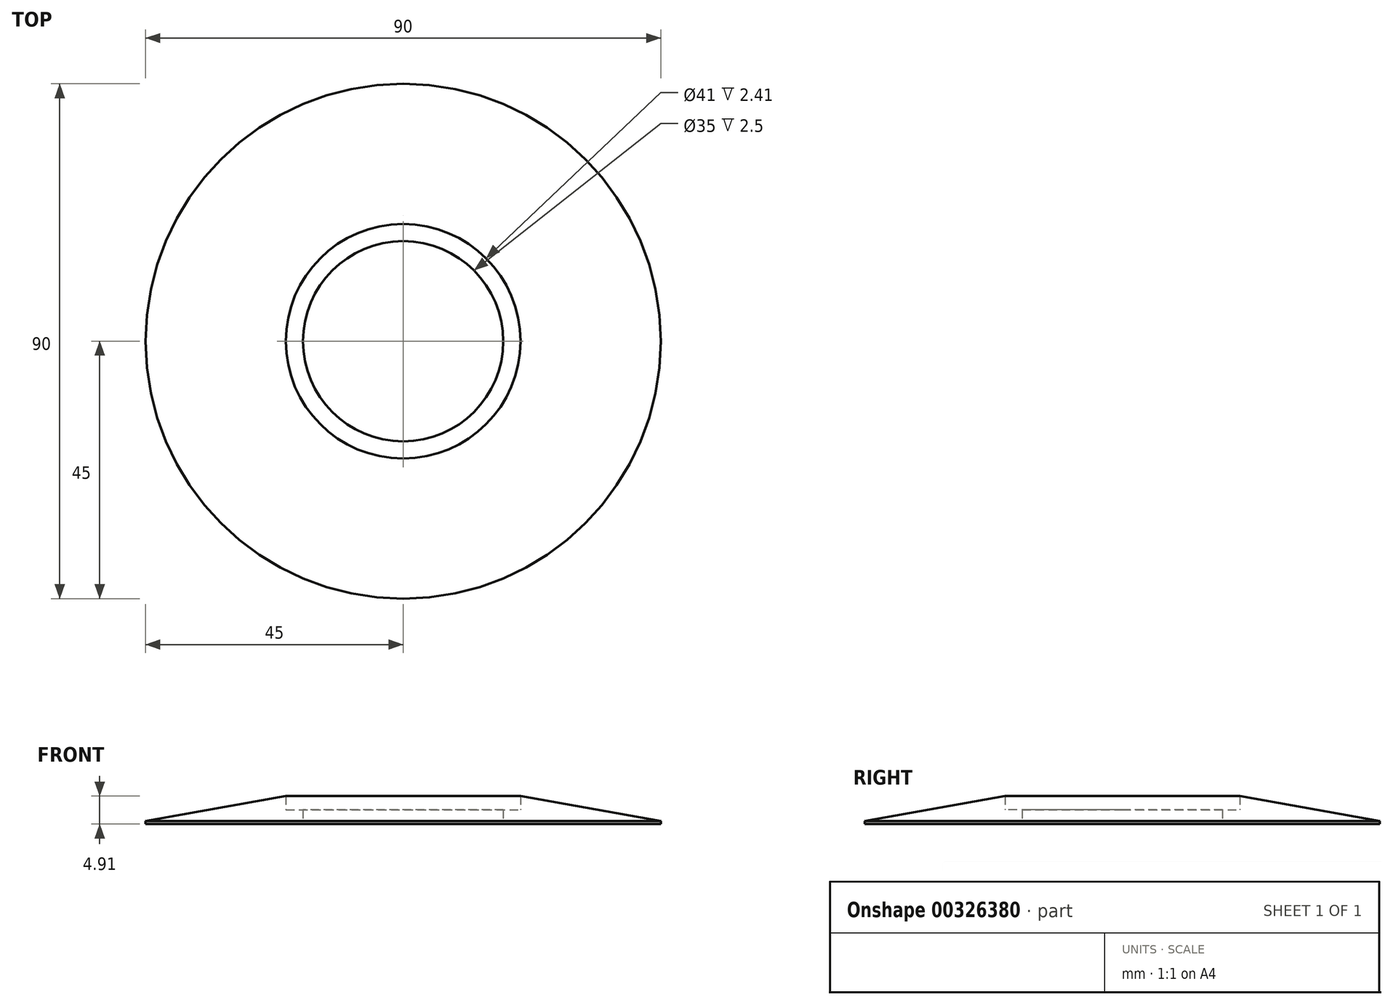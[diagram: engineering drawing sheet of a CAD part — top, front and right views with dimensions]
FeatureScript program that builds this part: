
annotation { "Feature Type Name" : "Feature", "Feature Type Description" : "" }
export const myFeature = defineFeature(function(context is Context, id is Id, definition is map)
    precondition{}
    {
        {
            var Q0;
            Q0=qCreatedBy(makeId("Top.planeOp"),FACE);
            var sketch = newSketch(context, id + "F0", { "sketchPlane" : qUnion([Q0])});
            skCircle(sketch, "E0", {"center": v(0, 0) * mm, "radius": 45 * mm});
            skCircle(sketch, "E1", {"center": v(0, 0) * mm, "radius": 20.5 * mm});
            skCircle(sketch, "E2", {"center": v(0, 0) * mm, "radius": 17.5 * mm});
            skSolve(sketch);
        }
        {
            var Q0;
            Q0=makeQuery(id+"F0.imprint","IMPRINT",FACE,{"disambiguationData":[TD([[makeQuery(id+"F0.imprint","IMPRINT",EDGE,{"derivedFrom":sQuery(id+"F0.wireOp",EDGE,"E0")}),1.0]])]});
            extrude(context, id + "F1", {"entities" : qUnion([Q0]), "depth" : 5 * mm});
        }
        {
            var Q0;
            Q0=makeQuery(id+"F0.imprint","IMPRINT",FACE,{"disambiguationData":[TD([[makeQuery(id+"F0.imprint","IMPRINT",EDGE,{"derivedFrom":sQuery(id+"F0.wireOp",EDGE,"E1")}),1.0]])]});
            extrude(context, id + "F2", {"entities" : qUnion([Q0]), "operationType" : NewBodyOperationType.ADD, "depth" : 2.5 * mm});
        }
        {
            var Q0;
            Q0=makeQuery(id+"F1.opExtrude","CAP_EDGE",EDGE,{"disambiguationData":[OSD([sQuery(id+"F0.wireOp",EDGE,"E0")])],"isStart":false});
            chamfer(context, id + "F3", {"entities" : qUnion([Q0]), "chamferType" : ChamferType.TWO_OFFSETS, "width1" : 25 * mm, "oppositeDirection" : false, "width2" : 4.5 * mm, "tangentPropagation" : true});
        }
    });
